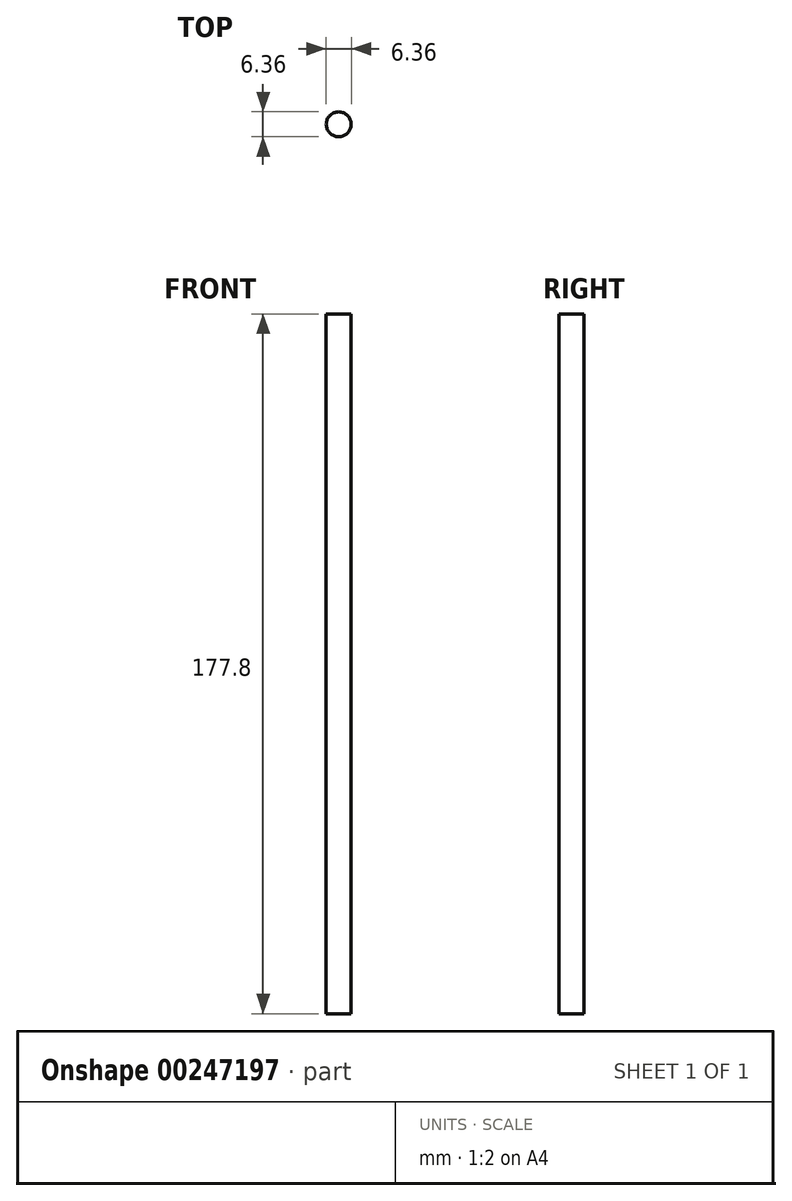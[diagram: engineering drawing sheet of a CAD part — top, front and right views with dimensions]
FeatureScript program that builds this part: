
annotation { "Feature Type Name" : "Feature", "Feature Type Description" : "" }
export const myFeature = defineFeature(function(context is Context, id is Id, definition is map)
    precondition{}
    {
        {
            var Q0;
            Q0=qCreatedBy(makeId("Top.planeOp"),FACE);
            var sketch = newSketch(context, id + "F0", { "sketchPlane" : qUnion([Q0])});
            skCircle(sketch, "E0", {"center": v(0, 0) * mm, "radius": 3.18 * mm});
            skSolve(sketch);
        }
        {
            var Q0;
            Q0 = qSketchRegion(id + "F0", true);
            extrude(context, id + "F1", {"entities" : qUnion([Q0]), "depth" : 177.8 * mm});
        }
    });
